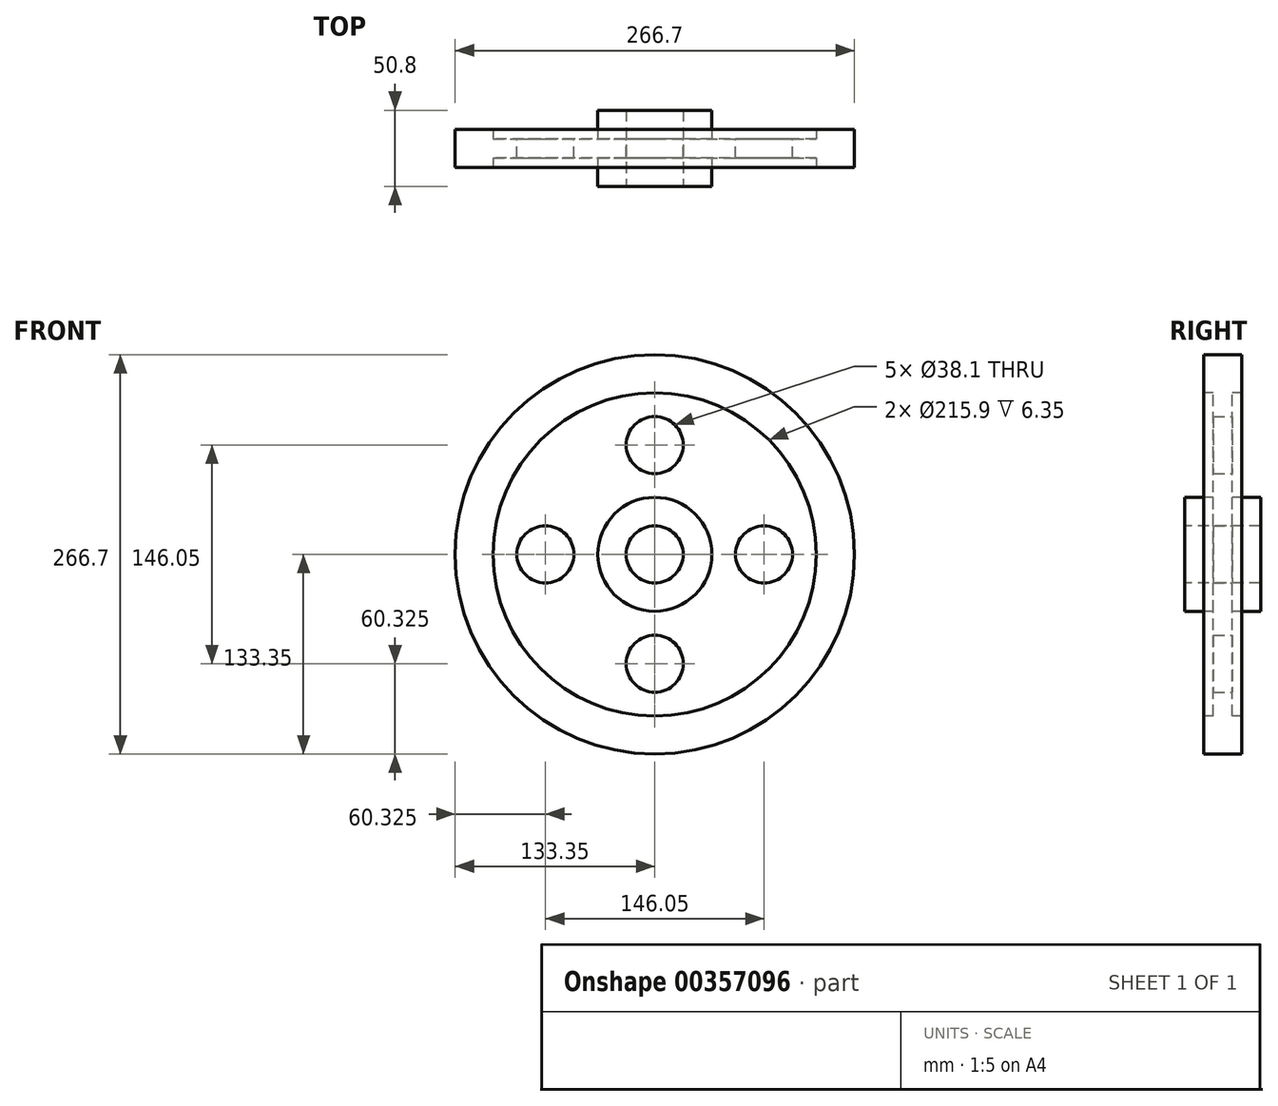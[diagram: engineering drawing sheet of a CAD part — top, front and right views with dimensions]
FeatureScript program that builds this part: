
annotation { "Feature Type Name" : "Feature", "Feature Type Description" : "" }
export const myFeature = defineFeature(function(context is Context, id is Id, definition is map)
    precondition{}
    {
        {
            var Q0;
            Q0=qCreatedBy(makeId("Right.planeOp"),FACE);
            var sketch = newSketch(context, id + "F0", { "sketchPlane" : qUnion([Q0])});
            skLineSegment(sketch, "E0", {"start": v(0, 0) * mm, "end": v(25.4, 0) * mm});
            skLineSegment(sketch, "E1.0", {"start": v(0, 19.05) * mm, "end": v(25.4, 19.05) * mm});
            skLineSegment(sketch, "E2.0", {"start": v(6.35, 107.95) * mm, "end": v(12.7, 107.95) * mm});
            skLineSegment(sketch, "E3.0", {"start": v(6.35, 38.1) * mm, "end": v(25.4, 38.1) * mm});
            skLineSegment(sketch, "E4", {"start": v(0, 133.35) * mm, "end": v(0, 19.05) * mm});
            skLineSegment(sketch, "E5.0", {"start": v(6.35, 107.95) * mm, "end": v(6.35, 38.1) * mm});
            skLineSegment(sketch, "E6.0", {"start": v(12.7, 133.35) * mm, "end": v(12.7, 107.95) * mm});
            skLineSegment(sketch, "E7", {"start": v(12.7, 133.35) * mm, "end": v(0, 133.35) * mm});
            skLineSegment(sketch, "E8", {"start": v(25.4, 38.1) * mm, "end": v(25.4, 19.05) * mm});
            skLineSegment(sketch, "E9.MirrorCS", {"start": v(-25.4, 38.1) * mm, "end": v(-25.4, 19.05) * mm});
            skLineSegment(sketch, "E10.MirrorCS", {"start": v(-6.35, 107.95) * mm, "end": v(-6.35, 38.1) * mm});
            skLineSegment(sketch, "E11.MirrorCS", {"start": v(-12.7, 133.35) * mm, "end": v(-12.7, 107.95) * mm});
            skLineSegment(sketch, "E12.MirrorCS", {"start": v(-12.7, 133.35) * mm, "end": v(0, 133.35) * mm});
            skLineSegment(sketch, "E13.MirrorCS", {"start": v(0, 19.05) * mm, "end": v(-25.4, 19.05) * mm});
            skLineSegment(sketch, "E14.MirrorCS", {"start": v(-6.35, 38.1) * mm, "end": v(-25.4, 38.1) * mm});
            skLineSegment(sketch, "E15.MirrorCS", {"start": v(-6.35, 107.95) * mm, "end": v(-12.7, 107.95) * mm});
            skSolve(sketch);
        }
        {
            var Q0;
            Q0=makeQuery(id+"F0.imprint","IMPRINT",FACE,{"disambiguationData":[TD([[makeQuery(id+"F0.imprint","IMPRINT",EDGE,{"derivedFrom":sQuery(id+"F0.wireOp",EDGE,"E4")}),-1.0]])]});
            var Q1;
            Q1=makeQuery(id+"F0.imprint","IMPRINT",FACE,{"disambiguationData":[TD([[makeQuery(id+"F0.imprint","IMPRINT",EDGE,{"derivedFrom":sQuery(id+"F0.wireOp",EDGE,"E1.0")}),1.0]])]});
            var Q2;
            Q2=sQuery(id+"F0.wireOp",EDGE,"E0");
            revolve(context, id + "F1", {"entities" : qUnion([Q0, Q1]), "axis" : qUnion([Q2]), "revolveType" : RevolveType.FULL});
        }
        {
            var Q0;
            Q0=makeQuery(id+"F1.opRevolve","SWEPT_FACE",FACE,{"disambiguationData":[OSD([sQuery(id+"F0.wireOp",EDGE,"E5.0")])]});
            var sketch = newSketch(context, id + "F2", { "sketchPlane" : qUnion([Q0])});
            skLineSegment(sketch, "E16", {"start": v(0, 0) * mm, "end": v(0, 73.03) * mm});
            skCircle(sketch, "E17", {"center": v(0, 73.03) * mm, "radius": 19.05 * mm});
            skCircle(sketch, "E18.1.0", {"center": v(-73.03, 0) * mm, "radius": 19.05 * mm});
            skCircle(sketch, "E18.2.0", {"center": v(0, -73.03) * mm, "radius": 19.05 * mm});
            skCircle(sketch, "E18.3.0", {"center": v(73.03, 0) * mm, "radius": 19.05 * mm});
            skPoint(sketch, "E18.center", {"position": v(0, 0) * mm});
            skSolve(sketch);
        }
        {
            var Q0;
            Q0=makeQuery(id+"F2.imprint","IMPRINT",FACE,{"disambiguationData":[TD([[makeQuery(id+"F2.imprint","IMPRINT",EDGE,{"derivedFrom":sQuery(id+"F2.wireOp",EDGE,"E18.3.0")}),1.0]])]});
            var Q1;
            Q1=makeQuery(id+"F2.imprint","IMPRINT",FACE,{"disambiguationData":[TD([[makeQuery(id+"F2.imprint","IMPRINT",EDGE,{"derivedFrom":sQuery(id+"F2.wireOp",EDGE,"E18.2.0")}),1.0]])]});
            var Q2;
            Q2=makeQuery(id+"F2.imprint","IMPRINT",FACE,{"disambiguationData":[TD([[makeQuery(id+"F2.imprint","IMPRINT",EDGE,{"derivedFrom":sQuery(id+"F2.wireOp",EDGE,"E18.1.0")}),1.0]])]});
            var Q3;
            Q3=makeQuery(id+"F2.imprint","IMPRINT",FACE,{"disambiguationData":[TD([[makeQuery(id+"F2.imprint","IMPRINT",EDGE,{"derivedFrom":sQuery(id+"F2.wireOp",EDGE,"E17")}),1.0]])]});
            extrude(context, id + "F3", {"entities" : qUnion([Q0, Q1, Q2, Q3]), "operationType" : NewBodyOperationType.REMOVE, "oppositeDirection" : true, "depth" : 25.4 * mm});
        }
    });
